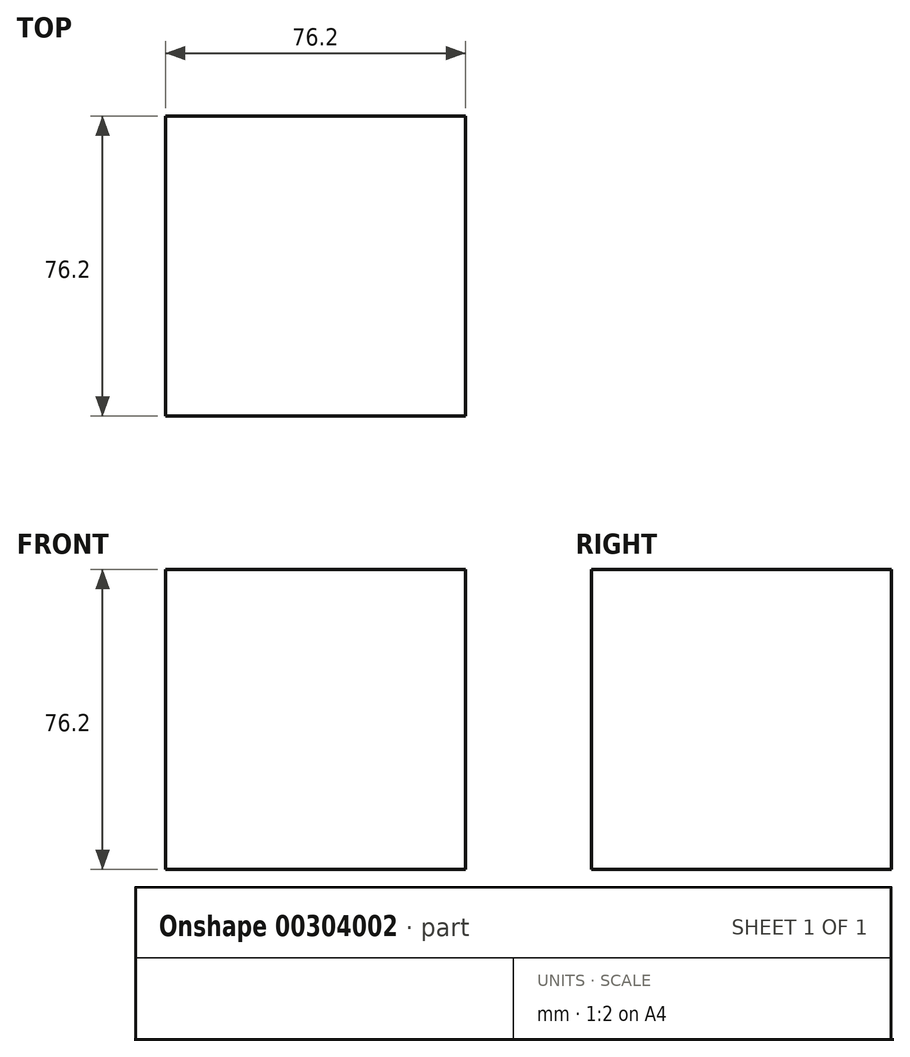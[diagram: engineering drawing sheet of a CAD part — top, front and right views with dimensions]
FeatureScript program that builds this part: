
annotation { "Feature Type Name" : "Feature", "Feature Type Description" : "" }
export const myFeature = defineFeature(function(context is Context, id is Id, definition is map)
    precondition{}
    {
        {
            var Q0;
            Q0=qCreatedBy(makeId("Top.planeOp"),FACE);
            var sketch = newSketch(context, id + "F0", { "sketchPlane" : qUnion([Q0])});
            skLineSegment(sketch, "E0.bottom", {"start": v(38.1, -38.1) * mm, "end": v(-38.1, -38.1) * mm});
            skLineSegment(sketch, "E0.top", {"start": v(38.1, 38.1) * mm, "end": v(-38.1, 38.1) * mm});
            skLineSegment(sketch, "E0.left", {"start": v(38.1, -38.1) * mm, "end": v(38.1, 38.1) * mm});
            skLineSegment(sketch, "E0.right", {"start": v(-38.1, -38.1) * mm, "end": v(-38.1, 38.1) * mm});
            skPoint(sketch, "E0.middle", {"position": v(0, 0) * mm});
            skSolve(sketch);
        }
        {
            var Q0;
            Q0 = qSketchRegion(id + "F0", true);
            extrude(context, id + "F1", {"entities" : qUnion([Q0]), "endBound" : BoundingType.SYMMETRIC, "depth" : 76.2 * mm});
        }
    });
